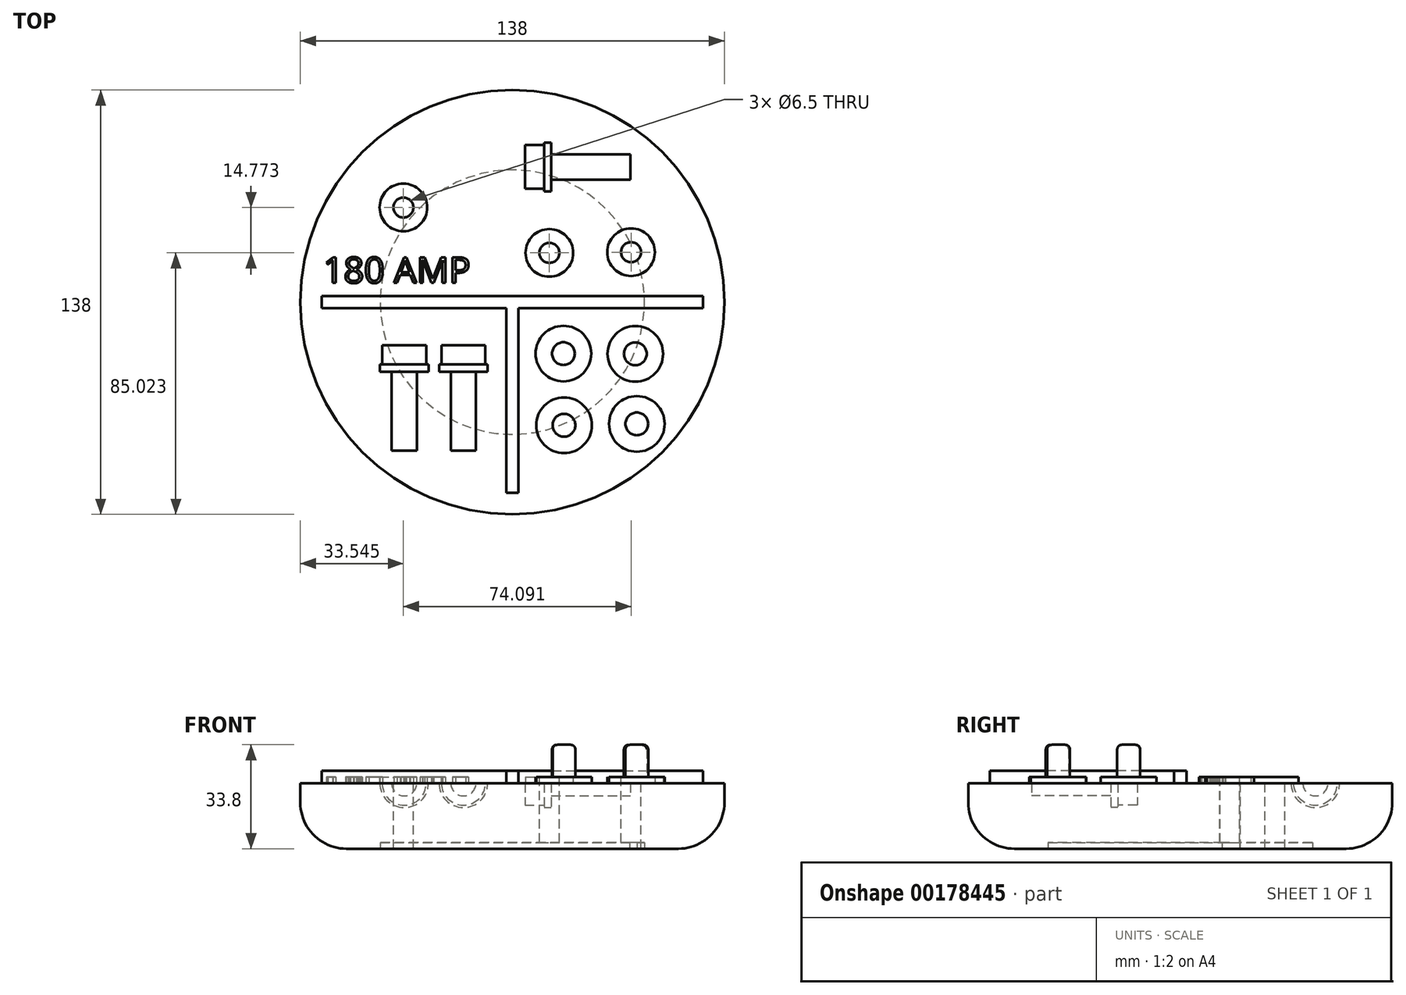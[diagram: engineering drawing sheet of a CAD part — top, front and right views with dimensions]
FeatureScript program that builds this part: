
annotation { "Feature Type Name" : "Feature", "Feature Type Description" : "" }
export const myFeature = defineFeature(function(context is Context, id is Id, definition is map)
    precondition{}
    {
        {
            var Q0;
            Q0=qCreatedBy(makeId("Front.planeOp"),FACE);
            var sketch = newSketch(context, id + "F0", { "sketchPlane" : qUnion([Q0])});
            skLineSegment(sketch, "E0.bottom", {"start": v(0, 0) * mm, "end": v(-69, 0) * mm});
            skLineSegment(sketch, "E0.top", {"start": v(0, -21.3) * mm, "end": v(-54, -21.3) * mm});
            skLineSegment(sketch, "E0.left", {"start": v(0, 0) * mm, "end": v(0, -21.3) * mm});
            skLineSegment(sketch, "E0.right", {"start": v(-69, 0) * mm, "end": v(-69, -6.3) * mm});
            skLineSegment(sketch, "E1.bottom", {"start": v(0, -21.3) * mm, "end": v(-43, -21.3) * mm});
            skLineSegment(sketch, "E1.top", {"start": v(0, -19.3) * mm, "end": v(-43, -19.3) * mm});
            skLineSegment(sketch, "E1.left", {"start": v(0, -21.3) * mm, "end": v(0, -19.3) * mm});
            skLineSegment(sketch, "E1.right", {"start": v(-43, -21.3) * mm, "end": v(-43, -19.3) * mm});
            skPoint(sketch, "E2.visualSharp", {"position": v(-69, -21.3) * mm});
            skArc(sketch, "E2.filletArc", {"start": v(-69, -6.3) * mm, "mid": v(-64.6, -16.9) * mm, "end": v(-54, -21.3) * mm});
            skSolve(sketch);
        }
        {
            var Q0;
            Q0 = qSketchRegion(id + "F0", true);
            var Q1;
            Q1=sQuery(id+"F0.wireOp",EDGE,"E1.left");
            revolve(context, id + "F1", {"entities" : qUnion([Q0]), "axis" : qUnion([Q1]), "revolveType" : RevolveType.FULL});
        }
        {
            var Q0;
            Q0=makeQuery(id+"F1.opRevolve","SWEPT_FACE",FACE,{"disambiguationData":[OSD([sQuery(id+"F0.wireOp",EDGE,"E0.top"),sQuery(id+"F0.wireOp",EDGE,"E1.bottom")])]});
            var sketch = newSketch(context, id + "F2", { "sketchPlane" : qUnion([Q0])});
            skCircle(sketch, "E3", {"center": v(0, 0) * mm, "radius": 43 * mm});
            skSolve(sketch);
        }
        {
            var Q0;
            Q0=makeQuery(id+"F2.imprint","IMPRINT",FACE,{"disambiguationData":[TD([[makeQuery(id+"F2.imprint","IMPRINT",EDGE,{"derivedFrom":sQuery(id+"F2.wireOp",EDGE,"E3")}),1.0]])]});
            extrude(context, id + "F3", {"entities" : qUnion([Q0]), "operationType" : NewBodyOperationType.REMOVE, "oppositeDirection" : true, "depth" : 2 * mm});
        }
        {
            var Q0;
            Q0=makeQuery(id+"F1.opRevolve","SWEPT_FACE",FACE,{"disambiguationData":[OSD([sQuery(id+"F0.wireOp",EDGE,"E0.bottom")])]});
            var sketch = newSketch(context, id + "F4", { "sketchPlane" : qUnion([Q0])});
            skLineSegment(sketch, "E4", {"start": v(0, 0) * mm, "end": v(0, -69) * mm, "construction": true});
            skLineSegment(sketch, "E5.bottom", {"start": v(-2, 0.01) * mm, "end": v(2, 0.01) * mm});
            skLineSegment(sketch, "E5.top", {"start": v(-2, -61.99) * mm, "end": v(2, -61.99) * mm});
            skLineSegment(sketch, "E5.left", {"start": v(-2, 0.01) * mm, "end": v(-2, -61.99) * mm});
            skLineSegment(sketch, "E5.right", {"start": v(2, 0.01) * mm, "end": v(2, -61.99) * mm});
            skLineSegment(sketch, "E6.bottom", {"start": v(-62.02, 2) * mm, "end": v(61.99, 2) * mm});
            skLineSegment(sketch, "E6.top", {"start": v(-62.02, -2) * mm, "end": v(61.99, -2) * mm});
            skLineSegment(sketch, "E6.left", {"start": v(-62.02, 2) * mm, "end": v(-62.02, -2) * mm});
            skLineSegment(sketch, "E6.right", {"start": v(61.99, 2) * mm, "end": v(61.99, -2) * mm});
            skSolve(sketch);
        }
        {
            var Q0;
            {var subQ1=sQuery(id+"F4.wireOp",EDGE,"E5.bottom");Q0=makeQuery(id+"F4.imprint","IMPRINT",FACE,{"disambiguationData":[TD([[makeQuery(id+"F4.imprint","IMPRINT",EDGE,{"derivedFrom":subQ1}),1.0]])]});}
            var Q1;
            Q1 = qSketchRegion(id + "F4", true);
            extrude(context, id + "F5", {"entities" : qUnion([Q0, Q1]), "operationType" : NewBodyOperationType.ADD, "depth" : 4 * mm});
        }
        {
            var Q0;
            Q0=makeQuery(id+"F1.opRevolve","SWEPT_FACE",FACE,{"disambiguationData":[OSD([sQuery(id+"F0.wireOp",EDGE,"E0.bottom")])]});
            var sketch = newSketch(context, id + "F6", { "sketchPlane" : qUnion([Q0])});
            skText(sketch, "E7", { "text": "180 AMP", "fontName": "OpenSans-Regular.ttf"});
            const initialGuessF6  = {"E7": [-0.0616, 0.00625, 1, 0, 0.0084]};
            skSetInitialGuess(sketch, initialGuessF6);
            skSolve(sketch);
        }
        {
            var Q0;
            Q0 = qSketchRegion(id + "F6", true);
            extrude(context, id + "F7", {"entities" : qUnion([Q0]), "operationType" : NewBodyOperationType.ADD, "depth" : 2 * mm});
        }
        {
            var Q0;
            Q0=makeQuery(id+"F7.boolean.opBoolean","SPLIT",FACE,{"disambiguationData":[TD([makeQuery(id+"F1.opRevolve","SWEPT_FACE",FACE,{"disambiguationData":[OSD([sQuery(id+"F0.wireOp",EDGE,"E0.right")])]})])],"derivedFrom":makeQuery(id+"F1.opRevolve","SWEPT_FACE",FACE,{"disambiguationData":[OSD([sQuery(id+"F0.wireOp",EDGE,"E0.bottom")])]})});
            var sketch = newSketch(context, id + "F8", { "sketchPlane" : qUnion([Q0])});
            skCircle(sketch, "E8", {"center": v(-35.45, 30.8) * mm, "radius": 7.75 * mm});
            skSolve(sketch);
        }
        {
            var Q0;
            Q0=makeQuery(id+"F8.imprint","IMPRINT",FACE,{"disambiguationData":[TD([[makeQuery(id+"F8.imprint","IMPRINT",EDGE,{"derivedFrom":sQuery(id+"F8.wireOp",EDGE,"E8")}),1.0]])]});
            var sketch = newSketch(context, id + "F9", { "sketchPlane" : qUnion([Q0])});
            skSolve(sketch);
        }
        {
            var Q0;
            Q0=makeQuery(id+"F9.imprint","IMPRINT",FACE,{"disambiguationData":[TD([[makeQuery(id+"F9.imprint","IMPRINT",EDGE,{"derivedFrom":makeQuery(id+"F8.imprint","IMPRINT",EDGE,{"derivedFrom":sQuery(id+"F8.wireOp",EDGE,"E8")})}),1.0]])]});
            var Q1;
            Q1 = qConstructionFilter(qBodyType(qCreatedBy(id + "F9" ,EDGE), BodyType.WIRE), ConstructionObject.NO);
            extrude(context, id + "F10", {"entities" : qUnion([Q0]), "operationType" : NewBodyOperationType.ADD, "surfaceEntities" : qUnion([Q1]), "depth" : 2 * mm});
        }
        {
            var Q0;
            Q0=makeQuery(id+"F8.imprint","IMPRINT",FACE,{"disambiguationData":[TD([[makeQuery(id+"F8.imprint","IMPRINT",EDGE,{"derivedFrom":sQuery(id+"F8.wireOp",EDGE,"E8")}),1.0]])]});
            extrude(context, id + "F11", {"entities" : qUnion([Q0]), "operationType" : NewBodyOperationType.ADD, "depth" : 2 * mm});
        }
        {
            var Q0;
            Q0=makeQuery(id+"F10.opExtrude","CAP_FACE",FACE,{"disambiguationData":[OSD([sQuery(id+"F8.wireOp",EDGE,"E8")])],"isStart":false});
            var sketch = newSketch(context, id + "F12", { "sketchPlane" : qUnion([Q0])});
            skCircle(sketch, "E9", {"center": v(-35.45, 30.8) * mm, "radius": 3.25 * mm});
            skSolve(sketch);
        }
        {
            var Q0;
            Q0=makeQuery(id+"F12.imprint","IMPRINT",FACE,{"disambiguationData":[TD([[makeQuery(id+"F12.imprint","IMPRINT",EDGE,{"derivedFrom":sQuery(id+"F12.wireOp",EDGE,"E9")}),1.0]])]});
            extrude(context, id + "F13", {"entities" : qUnion([Q0]), "operationType" : NewBodyOperationType.REMOVE, "endBound" : BoundingType.THROUGH_ALL, "oppositeDirection" : true, "depth" : 25 * mm});
        }
        {
            var Q0;
            Q0=makeQuery(id+"F7.boolean.opBoolean","SPLIT",FACE,{"disambiguationData":[TD([makeQuery(id+"F1.opRevolve","SWEPT_FACE",FACE,{"disambiguationData":[OSD([sQuery(id+"F0.wireOp",EDGE,"E0.right")])]})])],"derivedFrom":makeQuery(id+"F1.opRevolve","SWEPT_FACE",FACE,{"disambiguationData":[OSD([sQuery(id+"F0.wireOp",EDGE,"E0.bottom")])]})});
            var sketch = newSketch(context, id + "F14", { "sketchPlane" : qUnion([Q0])});
            skCircle(sketch, "E10", {"center": v(12.05, 16.02) * mm, "radius": 7.75 * mm});
            skSolve(sketch);
        }
        {
            var Q0;
            Q0 = qSketchRegion(id + "F14", true);
            extrude(context, id + "F15", {"entities" : qUnion([Q0]), "operationType" : NewBodyOperationType.ADD, "depth" : 2 * mm});
        }
        {
            var Q0;
            Q0=makeQuery(id+"F15.opExtrude","CAP_FACE",FACE,{"disambiguationData":[OSD([sQuery(id+"F14.wireOp",EDGE,"E10")])],"isStart":false});
            var sketch = newSketch(context, id + "F16", { "sketchPlane" : qUnion([Q0])});
            skCircle(sketch, "E11", {"center": v(12.05, 16.02) * mm, "radius": 3.25 * mm});
            skSolve(sketch);
        }
        {
            var Q0;
            Q0 = qSketchRegion(id + "F16", true);
            extrude(context, id + "F17", {"entities" : qUnion([Q0]), "operationType" : NewBodyOperationType.REMOVE, "endBound" : BoundingType.THROUGH_ALL, "oppositeDirection" : true, "depth" : 25 * mm});
        }
        {
            var Q0;
            Q0=makeQuery(id+"F7.boolean.opBoolean","SPLIT",FACE,{"disambiguationData":[TD([makeQuery(id+"F1.opRevolve","SWEPT_FACE",FACE,{"disambiguationData":[OSD([sQuery(id+"F0.wireOp",EDGE,"E0.right")])]})])],"derivedFrom":makeQuery(id+"F1.opRevolve","SWEPT_FACE",FACE,{"disambiguationData":[OSD([sQuery(id+"F0.wireOp",EDGE,"E0.bottom")])]})});
            var sketch = newSketch(context, id + "F18", { "sketchPlane" : qUnion([Q0])});
            skCircle(sketch, "E12", {"center": v(38.64, 16.25) * mm, "radius": 7.75 * mm});
            skSolve(sketch);
        }
        {
            var Q0;
            Q0 = qSketchRegion(id + "F18", true);
            extrude(context, id + "F19", {"entities" : qUnion([Q0]), "operationType" : NewBodyOperationType.ADD, "depth" : 2 * mm});
        }
        {
            var Q0;
            Q0=makeQuery(id+"F19.opExtrude","CAP_FACE",FACE,{"disambiguationData":[OSD([sQuery(id+"F18.wireOp",EDGE,"E12")])],"isStart":false});
            var sketch = newSketch(context, id + "F20", { "sketchPlane" : qUnion([Q0])});
            skCircle(sketch, "E13", {"center": v(38.64, 16.25) * mm, "radius": 3.25 * mm});
            skSolve(sketch);
        }
        {
            var Q0;
            Q0 = qSketchRegion(id + "F20", true);
            extrude(context, id + "F21", {"entities" : qUnion([Q0]), "operationType" : NewBodyOperationType.REMOVE, "endBound" : BoundingType.THROUGH_ALL, "oppositeDirection" : true, "depth" : 25 * mm});
        }
        {
            var Q0;
            Q0=makeQuery(id+"F7.boolean.opBoolean","SPLIT",FACE,{"disambiguationData":[TD([makeQuery(id+"F1.opRevolve","SWEPT_FACE",FACE,{"disambiguationData":[OSD([sQuery(id+"F0.wireOp",EDGE,"E0.right")])]})])],"derivedFrom":makeQuery(id+"F1.opRevolve","SWEPT_FACE",FACE,{"disambiguationData":[OSD([sQuery(id+"F0.wireOp",EDGE,"E0.bottom")])]})});
            var sketch = newSketch(context, id + "F22", { "sketchPlane" : qUnion([Q0])});
            skLineSegment(sketch, "E14", {"start": v(4.1, 43.98) * mm, "end": v(38.44, 43.98) * mm, "construction": true});
            skLineSegment(sketch, "E15.bottom", {"start": v(4.1, 43.98) * mm, "end": v(10.34, 43.98) * mm});
            skLineSegment(sketch, "E15.top", {"start": v(4.1, 36.85) * mm, "end": v(10.34, 36.85) * mm});
            skLineSegment(sketch, "E15.left", {"start": v(4.1, 43.98) * mm, "end": v(4.1, 36.85) * mm});
            skLineSegment(sketch, "E15.right", {"start": v(10.34, 40.41) * mm, "end": v(10.34, 36.85) * mm});
            skPoint(sketch, "E16.oppositeSnap0", {"position": v(10.34, 40.41) * mm});
            skLineSegment(sketch, "E16.bottom", {"start": v(10.34, 43.98) * mm, "end": v(12.7, 43.98) * mm});
            skLineSegment(sketch, "E16.top", {"start": v(10.34, 36.05) * mm, "end": v(12.7, 36.05) * mm});
            skLineSegment(sketch, "E16.left", {"start": v(10.34, 36.85) * mm, "end": v(10.34, 36.05) * mm});
            skLineSegment(sketch, "E16.right", {"start": v(12.7, 39.88) * mm, "end": v(12.7, 36.05) * mm});
            skLineSegment(sketch, "E17.bottom", {"start": v(12.7, 43.98) * mm, "end": v(38.44, 43.98) * mm});
            skLineSegment(sketch, "E17.top", {"start": v(12.7, 39.88) * mm, "end": v(38.44, 39.88) * mm});
            skLineSegment(sketch, "E17.right", {"start": v(38.44, 43.98) * mm, "end": v(38.44, 39.88) * mm});
            skPoint(sketch, "E18.orphan", {"position": v(0, 43.98) * mm});
            skSolve(sketch);
        }
        {
            var Q0;
            Q0=makeQuery(id+"F22.imprint","IMPRINT",FACE,{"disambiguationData":[TD([[makeQuery(id+"F22.imprint","IMPRINT",EDGE,{"derivedFrom":sQuery(id+"F22.wireOp",EDGE,"E15.bottom")}),-1.0]])]});
            var Q1;
            Q1=sQuery(id+"F22.wireOp",EDGE,"E17.bottom");
            revolve(context, id + "F23", {"operationType" : NewBodyOperationType.REMOVE, "entities" : qUnion([Q0]), "axis" : qUnion([Q1]), "revolveType" : RevolveType.FULL, "oppositeDirection" : true});
        }
        {
            var Q0;
            Q0=makeQuery(id+"F7.boolean.opBoolean","SPLIT",FACE,{"disambiguationData":[TD([makeQuery(id+"F1.opRevolve","SWEPT_FACE",FACE,{"disambiguationData":[OSD([sQuery(id+"F0.wireOp",EDGE,"E0.right")])]})])],"derivedFrom":makeQuery(id+"F1.opRevolve","SWEPT_FACE",FACE,{"disambiguationData":[OSD([sQuery(id+"F0.wireOp",EDGE,"E0.bottom")])]})});
            var sketch = newSketch(context, id + "F24", { "sketchPlane" : qUnion([Q0])});
            skLineSegment(sketch, "E19", {"start": v(-8.8, -14.01) * mm, "end": v(-15.93, -14.01) * mm, "construction": true});
            skLineSegment(sketch, "E20.left", {"start": v(-8.8, -14.01) * mm, "end": v(-8.8, -20.26) * mm, "construction": true});
            skLineSegment(sketch, "E20.right", {"start": v(-15.93, -14.01) * mm, "end": v(-15.93, -20.26) * mm, "construction": true});
            skLineSegment(sketch, "E21.bottom", {"start": v(-8.8, -20.26) * mm, "end": v(-8, -20.26) * mm, "construction": true});
            skLineSegment(sketch, "E21.top", {"start": v(-11.83, -22.61) * mm, "end": v(-8, -22.61) * mm, "construction": true});
            skLineSegment(sketch, "E21.left", {"start": v(-15.93, -20.26) * mm, "end": v(-15.93, -22.61) * mm, "construction": true});
            skLineSegment(sketch, "E21.right", {"start": v(-8, -20.26) * mm, "end": v(-8, -22.61) * mm, "construction": true});
            skLineSegment(sketch, "E22.top", {"start": v(-15.93, -48.36) * mm, "end": v(-11.83, -48.36) * mm});
            skLineSegment(sketch, "E22.left", {"start": v(-15.93, -22.61) * mm, "end": v(-15.93, -48.36) * mm});
            skLineSegment(sketch, "E22.right", {"start": v(-11.83, -22.61) * mm, "end": v(-11.83, -48.36) * mm});
            skLineSegment(sketch, "E23.bottom", {"start": v(-15.93, -14.01) * mm, "end": v(-8.8, -14.01) * mm});
            skLineSegment(sketch, "E23.left", {"start": v(-15.93, -14.01) * mm, "end": v(-15.93, -20.26) * mm});
            skLineSegment(sketch, "E23.right", {"start": v(-8.8, -14.01) * mm, "end": v(-8.8, -20.26) * mm});
            skLineSegment(sketch, "E24.bottom", {"start": v(-8, -20.26) * mm, "end": v(-8.8, -20.26) * mm});
            skLineSegment(sketch, "E24.top", {"start": v(-8, -22.61) * mm, "end": v(-11.83, -22.61) * mm});
            skLineSegment(sketch, "E24.left", {"start": v(-8, -20.26) * mm, "end": v(-8, -22.61) * mm});
            skLineSegment(sketch, "E24.right", {"start": v(-15.93, -20.26) * mm, "end": v(-15.93, -22.61) * mm});
            skSolve(sketch);
        }
        {
            var Q0;
            Q0 = qSketchRegion(id + "F24", true);
            var Q1;
            Q1=sQuery(id+"F24.wireOp",EDGE,"E22.left");
            revolve(context, id + "F25", {"operationType" : NewBodyOperationType.REMOVE, "entities" : qUnion([Q0]), "axis" : qUnion([Q1]), "revolveType" : RevolveType.FULL, "oppositeDirection" : true});
        }
        {
            var Q0;
            Q0=makeQuery(id+"F7.boolean.opBoolean","SPLIT",FACE,{"disambiguationData":[TD([makeQuery(id+"F1.opRevolve","SWEPT_FACE",FACE,{"disambiguationData":[OSD([sQuery(id+"F0.wireOp",EDGE,"E0.right")])]})])],"derivedFrom":makeQuery(id+"F1.opRevolve","SWEPT_FACE",FACE,{"disambiguationData":[OSD([sQuery(id+"F0.wireOp",EDGE,"E0.bottom")])]})});
            var sketch = newSketch(context, id + "F26", { "sketchPlane" : qUnion([Q0])});
            skLineSegment(sketch, "E25", {"start": v(-8.8, -14.01) * mm, "end": v(-54.14, -14.01) * mm, "construction": true});
            skLineSegment(sketch, "E26.bottom", {"start": v(-28.05, -14.01) * mm, "end": v(-35.2, -14.01) * mm, "construction": true});
            skLineSegment(sketch, "E26.left", {"start": v(-28.05, -14.01) * mm, "end": v(-28.05, -20.26) * mm, "construction": true});
            skLineSegment(sketch, "E26.right", {"start": v(-35.2, -14.01) * mm, "end": v(-35.2, -20.26) * mm, "construction": true});
            skLineSegment(sketch, "E27.bottom", {"start": v(-35.2, -14.01) * mm, "end": v(-28.05, -14.01) * mm});
            skLineSegment(sketch, "E27.left", {"start": v(-35.2, -14.01) * mm, "end": v(-35.2, -20.26) * mm});
            skLineSegment(sketch, "E27.right", {"start": v(-28.05, -14.01) * mm, "end": v(-28.05, -20.26) * mm});
            skLineSegment(sketch, "E28.bottom", {"start": v(-28.05, -20.26) * mm, "end": v(-27.28, -20.26) * mm});
            skLineSegment(sketch, "E28.top", {"start": v(-31.1, -22.61) * mm, "end": v(-27.28, -22.61) * mm});
            skLineSegment(sketch, "E28.left", {"start": v(-35.2, -20.26) * mm, "end": v(-35.2, -22.61) * mm});
            skLineSegment(sketch, "E28.right", {"start": v(-27.28, -20.26) * mm, "end": v(-27.28, -22.61) * mm});
            skLineSegment(sketch, "E29.top", {"start": v(-35.2, -48.36) * mm, "end": v(-31.1, -48.36) * mm});
            skLineSegment(sketch, "E29.left", {"start": v(-35.2, -22.61) * mm, "end": v(-35.2, -48.36) * mm});
            skLineSegment(sketch, "E29.right", {"start": v(-31.1, -22.61) * mm, "end": v(-31.1, -48.36) * mm});
            skSolve(sketch);
        }
        {
            var Q0;
            Q0 = qSketchRegion(id + "F26", true);
            var Q1;
            Q1=sQuery(id+"F26.wireOp",EDGE,"E29.left");
            revolve(context, id + "F27", {"operationType" : NewBodyOperationType.REMOVE, "entities" : qUnion([Q0]), "axis" : qUnion([Q1]), "revolveType" : RevolveType.FULL, "oppositeDirection" : true});
        }
        {
            var Q0;
            Q0=makeQuery(id+"F7.boolean.opBoolean","SPLIT",FACE,{"disambiguationData":[TD([makeQuery(id+"F1.opRevolve","SWEPT_FACE",FACE,{"disambiguationData":[OSD([sQuery(id+"F0.wireOp",EDGE,"E0.right")])]})])],"derivedFrom":makeQuery(id+"F1.opRevolve","SWEPT_FACE",FACE,{"disambiguationData":[OSD([sQuery(id+"F0.wireOp",EDGE,"E0.bottom")])]})});
            var sketch = newSketch(context, id + "F28", { "sketchPlane" : qUnion([Q0])});
            skCircle(sketch, "E30", {"center": v(16.62, -16.74) * mm, "radius": 9.05 * mm});
            skSolve(sketch);
        }
        {
            var Q0;
            Q0=makeQuery(id+"F28.imprint","IMPRINT",FACE,{"disambiguationData":[TD([[makeQuery(id+"F28.imprint","IMPRINT",EDGE,{"derivedFrom":sQuery(id+"F28.wireOp",EDGE,"E30")}),-1.0]])]});
            var sketch = newSketch(context, id + "F29", { "sketchPlane" : qUnion([Q0])});
            skCircle(sketch, "E31", {"center": v(40.02, -16.81) * mm, "radius": 9.05 * mm});
            skSolve(sketch);
        }
        {
            var Q0;
            Q0=makeQuery(id+"F28.imprint","IMPRINT",FACE,{"disambiguationData":[TD([[makeQuery(id+"F28.imprint","IMPRINT",EDGE,{"derivedFrom":sQuery(id+"F28.wireOp",EDGE,"E30")}),-1.0]])]});
            var sketch = newSketch(context, id + "F30", { "sketchPlane" : qUnion([Q0])});
            skCircle(sketch, "E32", {"center": v(16.82, -40.05) * mm, "radius": 9.05 * mm});
            skSolve(sketch);
        }
        {
            var Q0;
            Q0=makeQuery(id+"F28.imprint","IMPRINT",FACE,{"disambiguationData":[TD([[makeQuery(id+"F28.imprint","IMPRINT",EDGE,{"derivedFrom":sQuery(id+"F28.wireOp",EDGE,"E30")}),-1.0]])]});
            var sketch = newSketch(context, id + "F31", { "sketchPlane" : qUnion([Q0])});
            skCircle(sketch, "E33", {"center": v(40.51, -39.6) * mm, "radius": 9.05 * mm});
            skSolve(sketch);
        }
        {
            var Q0;
            Q0=makeQuery(id+"F28.imprint","IMPRINT",FACE,{"disambiguationData":[TD([[makeQuery(id+"F28.imprint","IMPRINT",EDGE,{"derivedFrom":sQuery(id+"F28.wireOp",EDGE,"E30")}),1.0]])]});
            extrude(context, id + "F32", {"entities" : qUnion([Q0]), "operationType" : NewBodyOperationType.ADD, "depth" : 2 * mm});
        }
        {
            var Q0;
            Q0=makeQuery(id+"F29.imprint","IMPRINT",FACE,{"disambiguationData":[TD([[makeQuery(id+"F29.imprint","IMPRINT",EDGE,{"derivedFrom":sQuery(id+"F29.wireOp",EDGE,"E31")}),1.0]])]});
            var Q1;
            Q1=makeQuery(id+"F30.imprint","IMPRINT",FACE,{"disambiguationData":[TD([[makeQuery(id+"F30.imprint","IMPRINT",EDGE,{"derivedFrom":sQuery(id+"F30.wireOp",EDGE,"E32")}),1.0]])]});
            extrude(context, id + "F33", {"entities" : qUnion([Q0, Q1]), "operationType" : NewBodyOperationType.ADD, "depth" : 2 * mm});
        }
        {
            var Q0;
            Q0=makeQuery(id+"F31.imprint","IMPRINT",FACE,{"disambiguationData":[TD([[makeQuery(id+"F31.imprint","IMPRINT",EDGE,{"derivedFrom":sQuery(id+"F31.wireOp",EDGE,"E33")}),1.0]])]});
            extrude(context, id + "F34", {"entities" : qUnion([Q0]), "operationType" : NewBodyOperationType.ADD, "depth" : 2 * mm});
        }
        {
            var Q0;
            Q0=makeQuery(id+"F32.opExtrude","CAP_FACE",FACE,{"disambiguationData":[OSD([sQuery(id+"F28.wireOp",EDGE,"E30")])],"isStart":false});
            var sketch = newSketch(context, id + "F35", { "sketchPlane" : qUnion([Q0])});
            skCircle(sketch, "E34", {"center": v(16.62, -16.74) * mm, "radius": 3.7 * mm});
            skSolve(sketch);
        }
        {
            var Q0;
            Q0=makeQuery(id+"F33.opExtrude","CAP_FACE",FACE,{"disambiguationData":[OSD([sQuery(id+"F30.wireOp",EDGE,"E32")])],"isStart":false});
            var sketch = newSketch(context, id + "F36", { "sketchPlane" : qUnion([Q0])});
            skCircle(sketch, "E35", {"center": v(16.82, -40.05) * mm, "radius": 3.7 * mm});
            skSolve(sketch);
        }
        {
            var Q0;
            Q0=makeQuery(id+"F34.opExtrude","CAP_FACE",FACE,{"disambiguationData":[OSD([sQuery(id+"F31.wireOp",EDGE,"E33")])],"isStart":false});
            var sketch = newSketch(context, id + "F37", { "sketchPlane" : qUnion([Q0])});
            skCircle(sketch, "E36", {"center": v(40.51, -39.6) * mm, "radius": 3.7 * mm});
            skSolve(sketch);
        }
        {
            var Q0;
            Q0=makeQuery(id+"F33.opExtrude","CAP_FACE",FACE,{"disambiguationData":[OSD([sQuery(id+"F29.wireOp",EDGE,"E31")])],"isStart":false});
            var sketch = newSketch(context, id + "F38", { "sketchPlane" : qUnion([Q0])});
            skCircle(sketch, "E37", {"center": v(40.02, -16.81) * mm, "radius": 3.7 * mm});
            skSolve(sketch);
        }
        {
            var Q0;
            Q0 = qSketchRegion(id + "F38", true);
            extrude(context, id + "F39", {"entities" : qUnion([Q0]), "operationType" : NewBodyOperationType.ADD, "depth" : 10.5 * mm});
        }
        {
            var Q0;
            Q0=makeQuery(id+"F35.imprint","IMPRINT",FACE,{"disambiguationData":[TD([[makeQuery(id+"F35.imprint","IMPRINT",EDGE,{"derivedFrom":sQuery(id+"F35.wireOp",EDGE,"E34")}),1.0]])]});
            var Q1;
            Q1=makeQuery(id+"F36.imprint","IMPRINT",FACE,{"disambiguationData":[TD([[makeQuery(id+"F36.imprint","IMPRINT",EDGE,{"derivedFrom":sQuery(id+"F36.wireOp",EDGE,"E35")}),1.0]])]});
            var Q2;
            Q2=makeQuery(id+"F37.imprint","IMPRINT",FACE,{"disambiguationData":[TD([[makeQuery(id+"F37.imprint","IMPRINT",EDGE,{"derivedFrom":sQuery(id+"F37.wireOp",EDGE,"E36")}),1.0]])]});
            extrude(context, id + "F40", {"entities" : qUnion([Q0, Q1, Q2]), "operationType" : NewBodyOperationType.ADD, "depth" : 10.5 * mm});
        }
        {
            var Q0;
            Q0=makeQuery(id+"F40.opExtrude","CAP_EDGE",EDGE,{"disambiguationData":[OSD([sQuery(id+"F36.wireOp",EDGE,"E35")])],"isStart":false});
            var Q1;
            Q1=makeQuery(id+"F40.opExtrude","CAP_EDGE",EDGE,{"disambiguationData":[OSD([sQuery(id+"F35.wireOp",EDGE,"E34")])],"isStart":false});
            var Q2;
            Q2=makeQuery(id+"F39.opExtrude","CAP_EDGE",EDGE,{"disambiguationData":[OSD([sQuery(id+"F38.wireOp",EDGE,"E37")])],"isStart":false});
            var Q3;
            Q3=makeQuery(id+"F40.opExtrude","CAP_EDGE",EDGE,{"disambiguationData":[OSD([sQuery(id+"F37.wireOp",EDGE,"E36")])],"isStart":false});
            fillet(context, id + "F41", {"entities" : qUnion([Q0, Q1, Q2, Q3]), "radius" : 1.5 * mm, "tangentPropagation" : true, "allowEdgeOverflow" : false});
        }
    });
